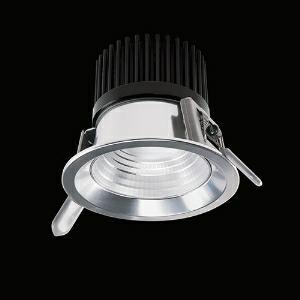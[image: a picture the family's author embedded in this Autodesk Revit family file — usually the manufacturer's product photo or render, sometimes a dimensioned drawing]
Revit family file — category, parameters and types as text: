
# Revit family: spectral_myral_myral_4500-840-m-dali
name_source: partatom
category: Lighting Fixtures
revit_build: Autodesk Revit 2016 (Build: 20150220_1215(x64)
units: mm (PartAtom-declared; Revit-internal decimal feet)

## family parameters
Cut with Voids When Loaded = No
Host = Face
Light Source = No
Part Type = Normal
Room Calculation Point = No
Round Connector Dimension = Use Diameter
Shared = No

## types (1)
- SPECTRAL MYRAL (1 x )
    Apparent Load = 0 VA
    Approval mark = CE
    CIE Flux Codes = 82 99 100 100 100
    Control Gear = Electronic transformer
    Default Elevation = 1800 mm
    Description = SPG0330183
MYRAL recessed spot

Design:
    Height = 0 mm  [stored 0 ft]
    Lamp = 1 x
    Lamp count = 1
    Length = 120 mm
    Luminous efficacy = 0 lm/W
    Manufacturer = Ridi
    ModVariant = No
    Model = MYRAL 4500-840-M-DALI
    Mounting Place = Ceiling
    Mounting Type = Recessed
    Number of Poles = 1
    OnlyDefault = Yes
    Power Factor = 1
    Product Name = SPECTRAL MYRAL
    Product group = Downlight recessed
    ProductGroupID = 400
    Protection Class = Protection class
    Protection Degree = IP 20
    RlxData = <blob elided: 38685 chars, md5=69e2163a>
    Socket = socket
    Standby Power = 0 W
    System Light Flux = 0 lm
    System Power = 0 W
    Type Image = myral_04.jpg
    URL = http://reluxnet.relux.com
    VarID = ---
    Voltage = 0 V
    Weight = 0.00 kg
    Width = 0 mm  [stored 0 ft]

note: [stored X ft] marks values corroborated as IEEE doubles in the binary element streams (Revit-internal decimal feet)

## geometry (parser evidence)
native form markers: Sweep x11
no freeform markers — native parametric forms only
